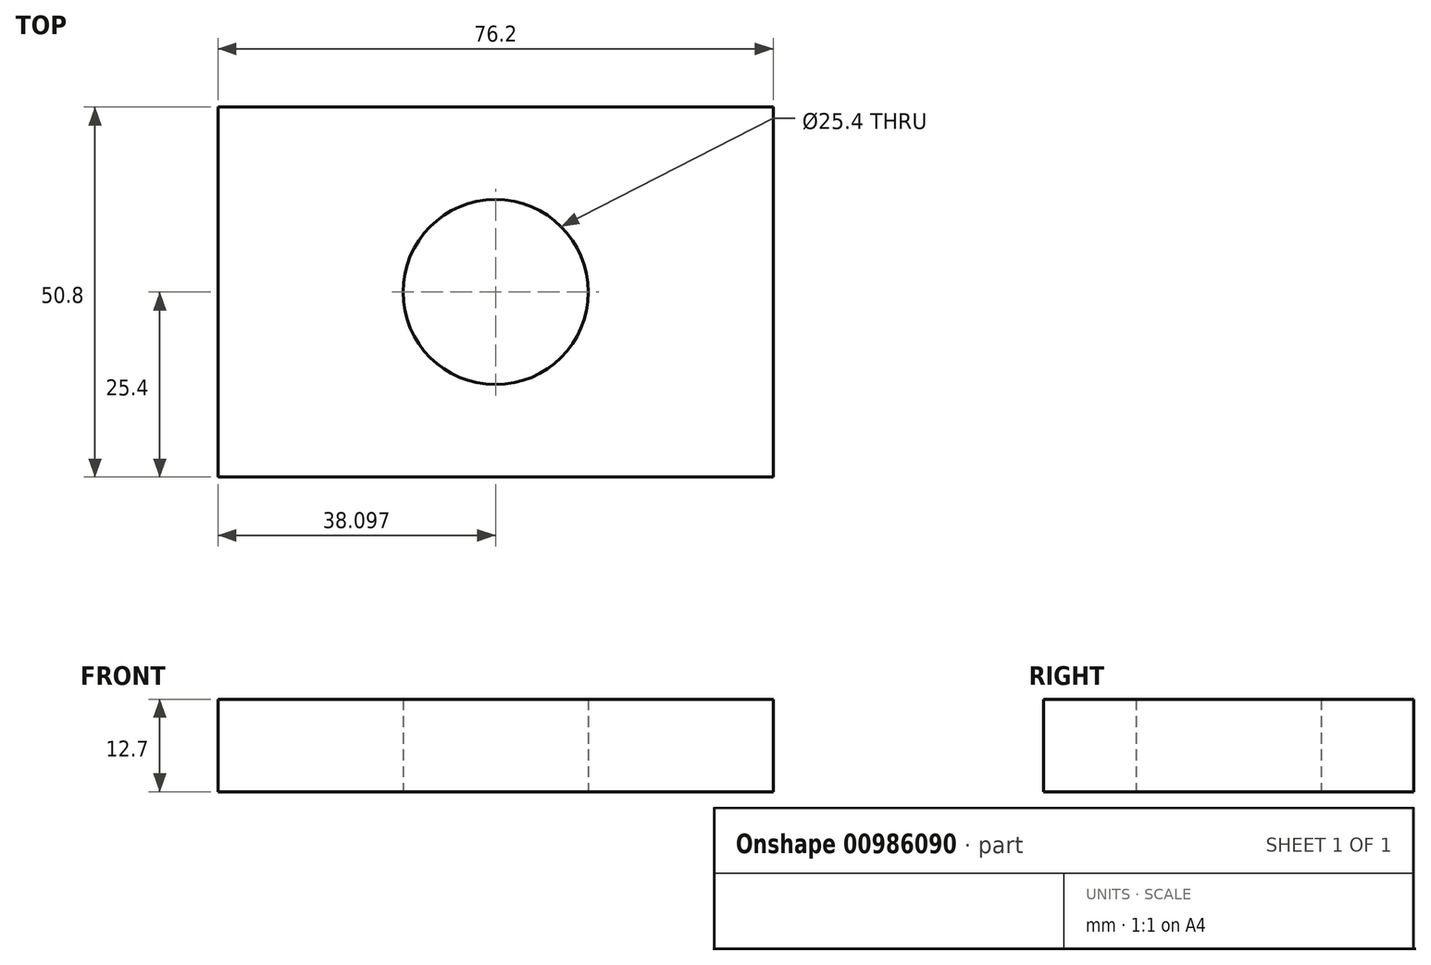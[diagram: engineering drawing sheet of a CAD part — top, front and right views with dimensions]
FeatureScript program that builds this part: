
annotation { "Feature Type Name" : "Feature", "Feature Type Description" : "" }
export const myFeature = defineFeature(function(context is Context, id is Id, definition is map)
    precondition{}
    {
        {
            var Q0;
            Q0=qCreatedBy(makeId("Top.planeOp"),FACE);
            var sketch = newSketch(context, id + "F0", { "sketchPlane" : qUnion([Q0])});
            skLineSegment(sketch, "E0.bottom", {"start": v(-46.66, -25.4) * mm, "end": v(29.54, -25.4) * mm});
            skLineSegment(sketch, "E0.top", {"start": v(-46.66, 25.4) * mm, "end": v(29.54, 25.4) * mm});
            skLineSegment(sketch, "E0.left", {"start": v(-46.66, -25.4) * mm, "end": v(-46.66, 25.4) * mm});
            skLineSegment(sketch, "E0.right", {"start": v(29.54, -25.4) * mm, "end": v(29.54, 25.4) * mm});
            skPoint(sketch, "E0.middle", {"position": v(-8.56, 0) * mm});
            skCircle(sketch, "E1", {"center": v(-8.56, 0) * mm, "radius": 12.7 * mm});
            skSolve(sketch);
        }
        {
            var Q0;
            Q0=makeQuery(id+"F0.imprint","IMPRINT",FACE,{"disambiguationData":[TD([[makeQuery(id+"F0.imprint","IMPRINT",EDGE,{"derivedFrom":sQuery(id+"F0.wireOp",EDGE,"E0.bottom")}),1.0]])]});
            extrude(context, id + "F1", {"entities" : qUnion([Q0]), "depth" : 12.7 * mm, "offsetDistance" : 25.4 * mm});
        }
    });
